# Revit family: LCAT-G
name_source: partatom
category: Lighting Fixtures
units: mm (PartAtom-declared; Revit-internal decimal feet)

## family parameters
Cut with Voids When Loaded = No
Host = Face
Light Source = No
OmniClass Number = 23.80.70.11
OmniClass Title = Luminaries for Internal Lighting
Part Type = Normal
Room Calculation Point = No
Round Connector Dimension = Use Diameter
Shared = No

## types (3) — shared parameters
Apparent Load = 0 VA
Default Elevation = 48"
Description = LCAT provides both design and value with an architectural appearance, LED technology to reduce maintenance and a wide range of options for classrooms, offices, retail and health care applications
Lamp = LED lamp
Manufacturer = Columbia Lighting
Model = LCAT-G
URL = https://www.currentlighting.com
Voltage = 120 V
Warranty = Five-year warranty
Wattage Comments = 40-80 W

## per-type parameters (varying)
| type | Backbox | Light Bulb | Load Classification | Photometric Web | Row Length | Width | zz Length |
| LCAT-G-14 | White Glass | White | Lighting | Web LCAT : LCAT14-30MLG-EDU | 48" | 12" | 47" |
| LCAT-G-22 | White | White Glass | Other | Web LCAT : LCAT22-40VLG-EDU | 24" | 24" | 23" |
| LCAT-G-24 | White | White Glass | Other | Web LCAT : LCAT24-40XLG-EDU | 48" | 25" | 47" |

## geometry (parser evidence)
native form markers: Sweep x6
no freeform markers — native parametric forms only
